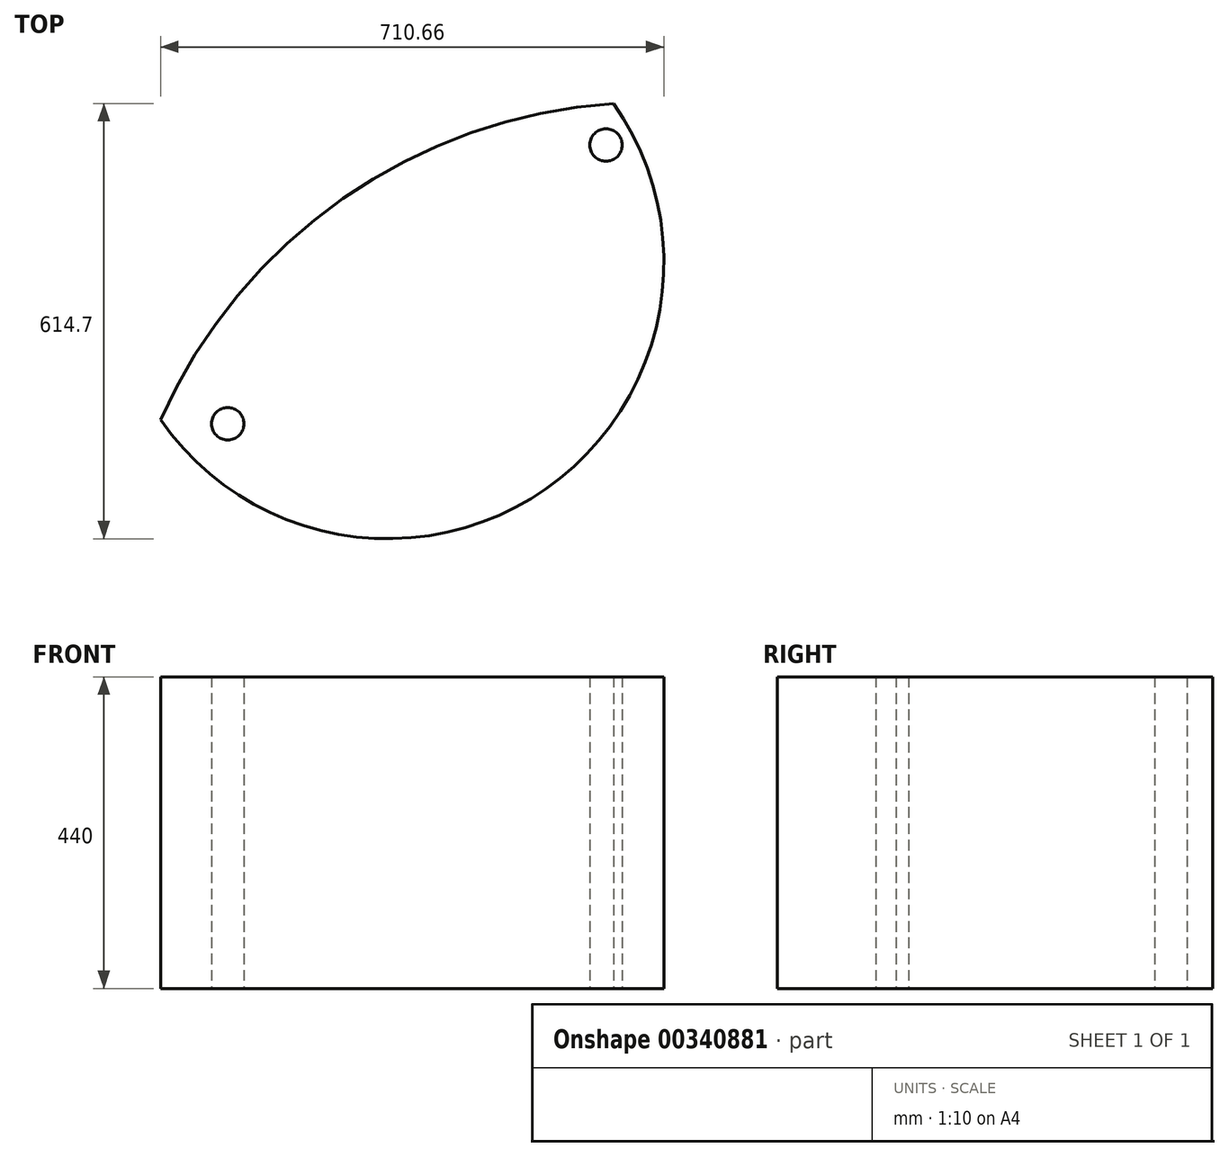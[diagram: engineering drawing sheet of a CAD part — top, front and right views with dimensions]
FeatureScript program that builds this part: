
annotation { "Feature Type Name" : "Feature", "Feature Type Description" : "" }
export const myFeature = defineFeature(function(context is Context, id is Id, definition is map)
    precondition{}
    {
        {
            var Q0;
            Q0=qCreatedBy(makeId("Top.planeOp"),FACE);
            var sketch = newSketch(context, id + "F0", { "sketchPlane" : qUnion([Q0])});
            skCircle(sketch, "E0.MirrorC", {"center": v(-505.06, -100.25) * mm, "radius": 22.91 * mm});
            skCircle(sketch, "E1.MirrorC", {"center": v(-74.52, -137) * mm, "radius": 22.91 * mm});
            skCircle(sketch, "E2.MirrorC", {"center": v(28.94, 293.34) * mm, "radius": 22.91 * mm});
            skArc(sketch, "E3", {"start": v(39.44, 352.09) * mm, "mid": v(-342.33, 217.57) * mm, "end": v(-600, -94.6) * mm});
            skArc(sketch, "E4", {"start": v(-600, -94.6) * mm, "mid": v(-56, -192.32) * mm, "end": v(39.44, 352.09) * mm});
            skSolve(sketch);
        }
        {
            var Q0;
            Q0=qSketchRegion(id+"F0",true);
            var Q1;
            Q1=makeQuery(id+"F0.imprint","IMPRINT",FACE,{"disambiguationData":[TD([[makeQuery(id+"F0.imprint","IMPRINT",EDGE,{"derivedFrom":sQuery(id+"F0.wireOp",EDGE,"E2.MirrorC")}),-1.0]])]});
            var Q2;
            Q2=makeQuery(id+"F0.imprint","IMPRINT",FACE,{"disambiguationData":[TD([[makeQuery(id+"F0.imprint","IMPRINT",EDGE,{"derivedFrom":sQuery(id+"F0.wireOp",EDGE,"E1.MirrorC")}),1.0]])]});
            var Q3;
            Q3=makeQuery(id+"F0.imprint","IMPRINT",FACE,{"disambiguationData":[TD([[makeQuery(id+"F0.imprint","IMPRINT",EDGE,{"derivedFrom":sQuery(id+"F0.wireOp",EDGE,"E0.MirrorC")}),-1.0]])]});
            var Q4;
            Q4=makeQuery(id+"F0.imprint","IMPRINT",FACE,{"disambiguationData":[TD([[makeQuery(id+"F0.imprint","IMPRINT",EDGE,{"derivedFrom":sQuery(id+"F0.wireOp",EDGE,"a83e4e48-81b9-4352-90c4-982a5ef1383d0.MirrorC")}),1.0]])]});
            extrude(context, id + "F1", {"entities" : qUnion([Q0, Q1, Q2, Q3, Q4]), "depth" : 40 * mm});
        }
        {
            var Q0;
            Q0=makeQuery(id+"F0.imprint","IMPRINT",FACE,{"disambiguationData":[TD([[makeQuery(id+"F0.imprint","IMPRINT",EDGE,{"derivedFrom":sQuery(id+"F0.wireOp",EDGE,"E0.MirrorC")}),-1.0]])]});
            var Q1;
            Q1=makeQuery(id+"F0.imprint","IMPRINT",FACE,{"disambiguationData":[TD([[makeQuery(id+"F0.imprint","IMPRINT",EDGE,{"derivedFrom":sQuery(id+"F0.wireOp",EDGE,"E1.MirrorC")}),1.0]])]});
            var Q2;
            Q2=makeQuery(id+"F0.imprint","IMPRINT",FACE,{"disambiguationData":[TD([[makeQuery(id+"F0.imprint","IMPRINT",EDGE,{"derivedFrom":sQuery(id+"F0.wireOp",EDGE,"E2.MirrorC")}),-1.0]])]});
            extrude(context, id + "F2", {"entities" : qUnion([Q0, Q1, Q2]), "operationType" : NewBodyOperationType.ADD, "oppositeDirection" : true, "depth" : 400 * mm});
        }
    });
